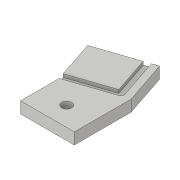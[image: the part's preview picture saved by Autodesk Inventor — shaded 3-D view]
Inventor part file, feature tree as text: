
AUTODESK INVENTOR PART (.ipt)
format: ipt  version: 2018.3 (Build 223284000, 284)  size: 108,544 bytes
history: native  units: in
note: dims shown in document units (in); Inventor stores cm internally (conversion verified against a paired STEP export)
features: extrude x2, sketch x2, fillet x1
ambient origin geometry x8: Origin, YZ Plane, XZ Plane, XY Plane, X Axis, Y Axis, Z Axis, Center Point
bodies: Solid1 (feature_tree)
feature tree (5):
  extrude  "Extrusion1"  Depth=0.221in
  extrude  "Extrusion2"  Depth=0.126in
  fillet  "Fillet1"  Radius=0.0625in
  sketch  "Sketch1"  dims[d0=0.75in d1=0.875in d2=1.1003in d3=1.0432in d4=0.1925in d5=0.221in d6=0.0in d10=0.125in]
  sketch  "Sketch2"  dims[d11=0.126in d12=0.126in d13=0.0625in d14=0.0in d15=0.0in d16=0.0625in]
